# Revit family: Vitra_M-LineSeries_Wall-HungWCPan_5671B003-0075
name_source: partatom
category: Plumbing Fixtures
revit_build: Autodesk Revit 2017 (Build: 20160225_1515(x64)
units: mm (PartAtom-declared; Revit-internal decimal feet)

## family parameters
Cut with Voids When Loaded = No
Host = Face
OmniClass Number = 23.45.05.21.11
OmniClass Title = Water Closets
Part Type = Normal
Room Calculation Point = No
Round Connector Dimension = Use Diameter
Shared = Yes

## types (1)
- WC_Wall-HungWCPan_Vitra_MLineSeries_5671B003-0075
    Article No. (default) = 5671B003-0075
    BIMobject category = Sanitary - Toilets
    CW Connection = Yes
    Color = White
    Cost = 0 $
    Default Elevation = 400 mm  [stored 1.31234 ft]
    Description = VitrA M-Line Wall-Hung WC Pan
    Design country = Turkey
    HW Connection = No
    IFC Classification = Sanitary Terminal
    Installation instructions = https://cdn.vitra.com.tr
    Main Material = Ceramic
    Manufacturer = Vitra
    Manufacturer name = Vitra
    Masterformat 2014 Code = 22 45 26
    Masterformat 2014 Description = Sanitary Facilities
    Model = 5671B003-0075
    MountingType = Wall Mounted
    NBS Referans Code = 35-65-90
    NBS Referans Description = Toilet Systems
    Nominal Depth (mm) = 490 mm  [stored 1.60761 ft]
    Nominal Height (mm) = 330 mm
    Nominal Width (mm) = 360 mm  [stored 1.1811 ft]
    OmniClass Code = 23-31 19 00
    OmniClass Description = Toilets
    Product Guid = https://cdn.vitra.com.tr
    Product SKU = 5671B003-0075
    Product certification = https://vitraglobal.com
    Product data url = https://www.vitra.co.uk
    Product family = M-Line
    Product group = Wall Mounted WC
    Secondary Material = Vitra-Ceramic-White
    Technical description = https://www.vitraglobal.com
    UNSPSC Code = 301815
    UNSPSC Description = Sanitary Ware
    URL = https://www.vitra.com.tr
    Uniclass 1.4 Code = L7216
    Uniclass 1.4 Description = Toilets
    Uniclass 2.0 Code = SS-35-65-90
    Uniclass 2.0 Description = Toilet Systems
    Uniclass 2015 Code = Pr_40_20_93
    Uniclass 2015 Name = Urinal and WC fittings
    Uniformat II Code = D2010
    Uniformat II Description = Sanitary Facilities
    Vent Connection = No
    Warranty Period (Year) = 10 Years
    Waste Connection = Yes
    Weight Net (kg) = 25,560
    Youtube = https://www.youtube.com

note: [stored X ft] marks values corroborated as IEEE doubles in the binary element streams (Revit-internal decimal feet)

## geometry (parser evidence)
native form markers: Sweep x3
no freeform markers — native parametric forms only
